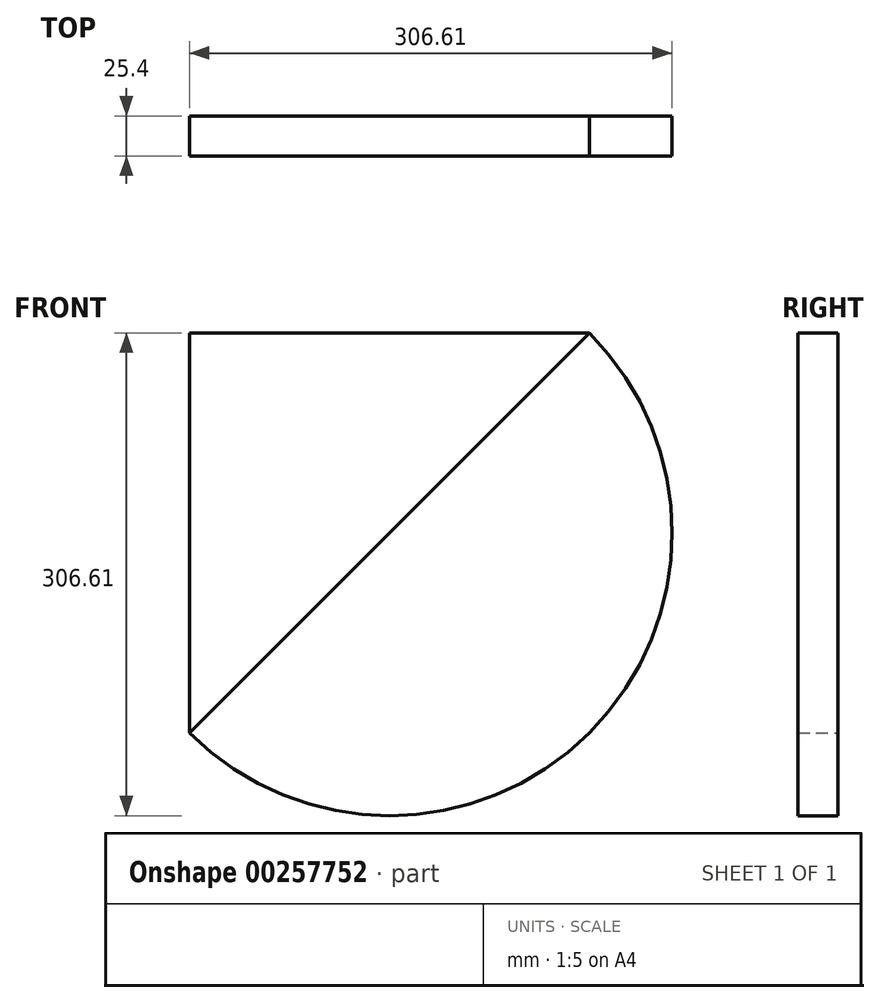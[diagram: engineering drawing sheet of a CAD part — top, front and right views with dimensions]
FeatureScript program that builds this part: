
annotation { "Feature Type Name" : "Feature", "Feature Type Description" : "" }
export const myFeature = defineFeature(function(context is Context, id is Id, definition is map)
    precondition{}
    {
        {
            var Q0;
            Q0=qCreatedBy(makeId("Front.planeOp"),FACE);
            var sketch = newSketch(context, id + "F0", { "sketchPlane" : qUnion([Q0])});
            skLineSegment(sketch, "E0.top", {"start": v(127, 127) * mm, "end": v(-127, 127) * mm});
            skLineSegment(sketch, "E0.right", {"start": v(-127, -127) * mm, "end": v(-127, 127) * mm});
            skPoint(sketch, "E0.middle", {"position": v(0, 0) * mm});
            skLineSegment(sketch, "E1", {"start": v(127, 127) * mm, "end": v(-127, -127) * mm});
            skArc(sketch, "E2", {"start": v(-127, -127) * mm, "mid": v(127, -127) * mm, "end": v(127, 127) * mm});
            skSolve(sketch);
        }
        {
            var Q0;
            Q0=makeQuery(id+"F0.imprint","IMPRINT",FACE,{"disambiguationData":[TD([[makeQuery(id+"F0.imprint","IMPRINT",EDGE,{"derivedFrom":sQuery(id+"F0.wireOp",EDGE,"E0.top")}),1.0]])]});
            extrude(context, id + "F1", {"entities" : qUnion([Q0]), "depth" : 25.4 * mm});
        }
        {
            var Q0;
            Q0=makeQuery(id+"F0.imprint","IMPRINT",FACE,{"disambiguationData":[TD([[makeQuery(id+"F0.imprint","IMPRINT",EDGE,{"derivedFrom":sQuery(id+"F0.wireOp",EDGE,"E1")}),1.0]])]});
            extrude(context, id + "F2", {"entities" : qUnion([Q0]), "depth" : 25.4 * mm});
        }
    });
